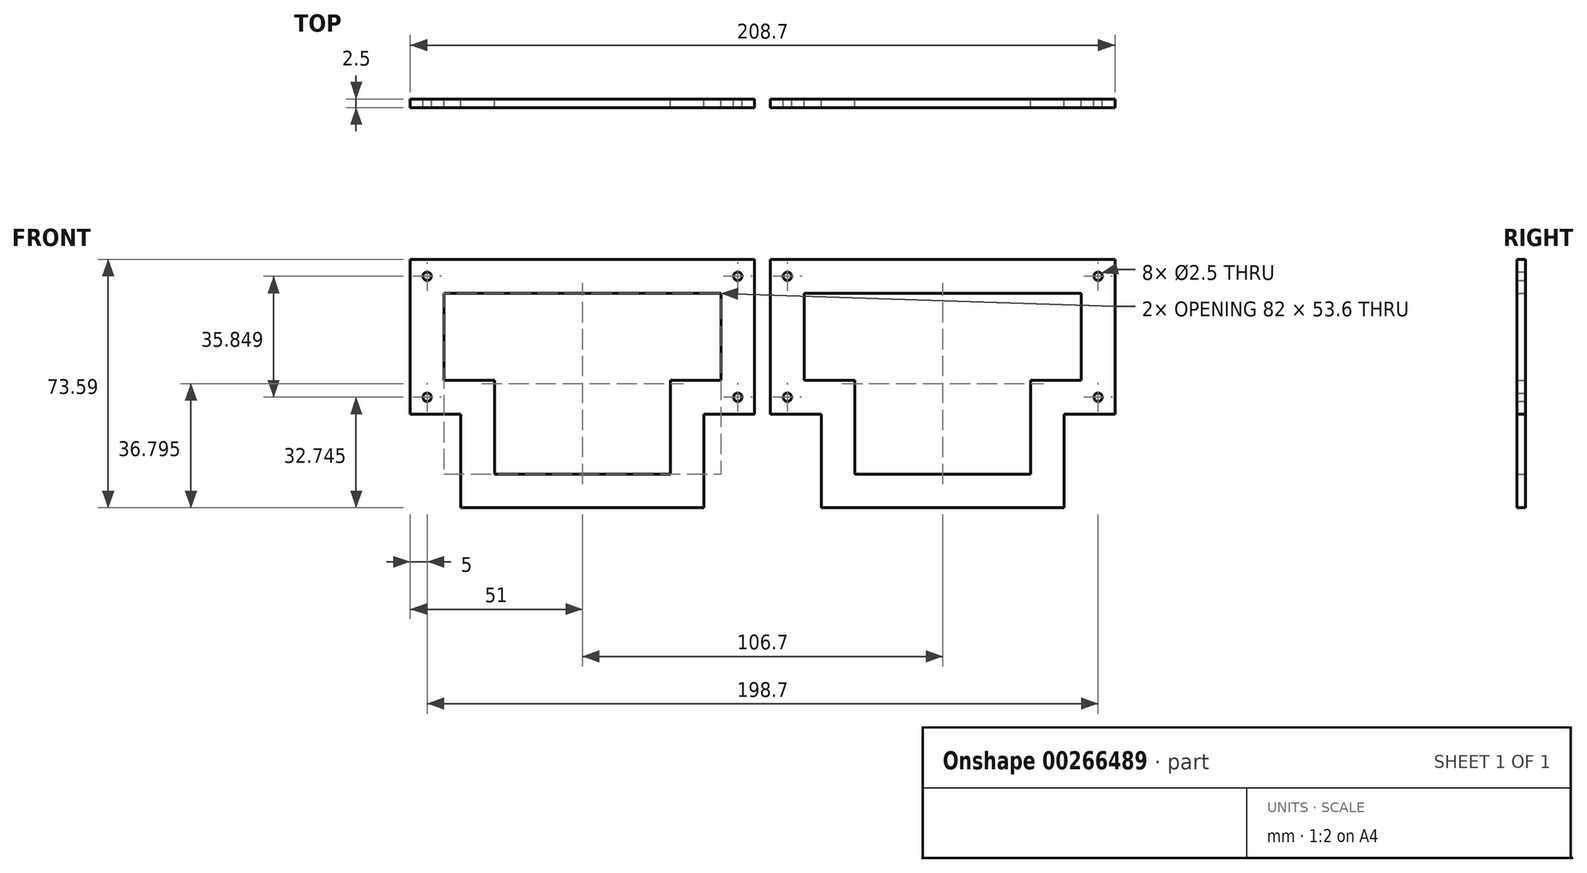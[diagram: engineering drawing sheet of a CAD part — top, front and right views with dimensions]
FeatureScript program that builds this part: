
annotation { "Feature Type Name" : "Feature", "Feature Type Description" : "" }
export const myFeature = defineFeature(function(context is Context, id is Id, definition is map)
    precondition{}
    {
        {
            var Q0;
            Q0=qCreatedBy(makeId("Front.planeOp"),FACE);
            var sketch = newSketch(context, id + "F0", { "sketchPlane" : qUnion([Q0])});
            skLineSegment(sketch, "E0", {"start": v(-36, -36.51) * mm, "end": v(36, -36.51) * mm});
            skLineSegment(sketch, "E1", {"start": v(36, -36.51) * mm, "end": v(36, -8.76) * mm});
            skLineSegment(sketch, "E2", {"start": v(36, -8.76) * mm, "end": v(51, -8.76) * mm});
            skLineSegment(sketch, "E3", {"start": v(51, -8.76) * mm, "end": v(51, 37.08) * mm});
            skLineSegment(sketch, "E4", {"start": v(51, 37.08) * mm, "end": v(-51, 37.08) * mm});
            skLineSegment(sketch, "E5", {"start": v(-51, 37.08) * mm, "end": v(-51, -8.76) * mm});
            skLineSegment(sketch, "E6", {"start": v(-51, -8.76) * mm, "end": v(-36, -8.76) * mm});
            skLineSegment(sketch, "E7", {"start": v(-36, -8.76) * mm, "end": v(-36, -36.51) * mm});
            skLineSegment(sketch, "E8.0", {"start": v(-26, -26.51) * mm, "end": v(26, -26.51) * mm});
            skLineSegment(sketch, "E8.1", {"start": v(-26, 1.24) * mm, "end": v(-26, -26.51) * mm});
            skLineSegment(sketch, "E8.2", {"start": v(26, -26.51) * mm, "end": v(26, 1.24) * mm});
            skLineSegment(sketch, "E8.3", {"start": v(-41, 1.24) * mm, "end": v(-26, 1.24) * mm});
            skLineSegment(sketch, "E8.4", {"start": v(26, 1.24) * mm, "end": v(41, 1.24) * mm});
            skLineSegment(sketch, "E8.5", {"start": v(41, 1.24) * mm, "end": v(41, 27.08) * mm});
            skLineSegment(sketch, "E8.6", {"start": v(41, 27.08) * mm, "end": v(-41, 27.08) * mm});
            skLineSegment(sketch, "E8.7", {"start": v(-41, 27.08) * mm, "end": v(-41, 1.24) * mm});
            skLineSegment(sketch, "E9", {"start": v(-51, 37.08) * mm, "end": v(-41, 27.08) * mm, "construction": true});
            skLineSegment(sketch, "E10", {"start": v(51, 37.08) * mm, "end": v(41, 27.08) * mm, "construction": true});
            skLineSegment(sketch, "E11", {"start": v(41, 1.24) * mm, "end": v(51, -8.76) * mm, "construction": true});
            skLineSegment(sketch, "E12", {"start": v(-41, 1.24) * mm, "end": v(-51, -8.76) * mm, "construction": true});
            skCircle(sketch, "E13", {"center": v(-46, 32.08) * mm, "radius": 1.25 * mm});
            skCircle(sketch, "E14", {"center": v(-46, -3.76) * mm, "radius": 1.25 * mm});
            skCircle(sketch, "E15", {"center": v(46, -3.76) * mm, "radius": 1.25 * mm});
            skCircle(sketch, "E16", {"center": v(46, 32.08) * mm, "radius": 1.25 * mm});
            skLineSegment(sketch, "E17.1.0.0", {"start": v(-132.7, 1.24) * mm, "end": v(-132.7, -26.51) * mm});
            skLineSegment(sketch, "E17.1.0.1", {"start": v(-132.7, -26.51) * mm, "end": v(-80.7, -26.51) * mm});
            skLineSegment(sketch, "E17.1.0.2", {"start": v(-65.7, 27.08) * mm, "end": v(-147.7, 27.08) * mm});
            skLineSegment(sketch, "E17.1.0.3", {"start": v(-142.7, -8.76) * mm, "end": v(-142.7, -36.51) * mm});
            skLineSegment(sketch, "E17.1.0.4", {"start": v(-147.7, 27.08) * mm, "end": v(-147.7, 1.24) * mm});
            skLineSegment(sketch, "E17.1.0.5", {"start": v(-65.7, 1.24) * mm, "end": v(-65.7, 27.08) * mm});
            skLineSegment(sketch, "E17.1.0.6", {"start": v(-70.7, -36.51) * mm, "end": v(-70.7, -8.76) * mm});
            skLineSegment(sketch, "E17.1.0.7", {"start": v(-157.7, 37.08) * mm, "end": v(-157.7, -8.76) * mm});
            skLineSegment(sketch, "E17.1.0.8", {"start": v(-142.7, -36.51) * mm, "end": v(-70.7, -36.51) * mm});
            skLineSegment(sketch, "E17.1.0.9", {"start": v(-80.7, -26.51) * mm, "end": v(-80.7, 1.24) * mm});
            skLineSegment(sketch, "E17.1.0.10", {"start": v(-147.7, 1.24) * mm, "end": v(-132.7, 1.24) * mm});
            skLineSegment(sketch, "E17.1.0.11", {"start": v(-80.7, 1.24) * mm, "end": v(-65.7, 1.24) * mm});
            skLineSegment(sketch, "E17.1.0.12", {"start": v(-147.7, 1.24) * mm, "end": v(-157.7, -8.76) * mm, "construction": true});
            skLineSegment(sketch, "E17.1.0.13", {"start": v(-70.7, -8.76) * mm, "end": v(-55.7, -8.76) * mm});
            skLineSegment(sketch, "E17.1.0.14", {"start": v(-157.7, -8.76) * mm, "end": v(-142.7, -8.76) * mm});
            skCircle(sketch, "E17.1.0.15", {"center": v(-152.7, 32.08) * mm, "radius": 1.25 * mm});
            skLineSegment(sketch, "E17.1.0.16", {"start": v(-157.7, 37.08) * mm, "end": v(-147.7, 27.08) * mm, "construction": true});
            skCircle(sketch, "E17.1.0.17", {"center": v(-152.7, -3.76) * mm, "radius": 1.25 * mm});
            skCircle(sketch, "E17.1.0.18", {"center": v(-60.7, -3.76) * mm, "radius": 1.25 * mm});
            skLineSegment(sketch, "E17.1.0.19", {"start": v(-65.7, 1.24) * mm, "end": v(-55.7, -8.76) * mm, "construction": true});
            skLineSegment(sketch, "E17.1.0.20", {"start": v(-55.7, -8.76) * mm, "end": v(-55.7, 37.08) * mm});
            skLineSegment(sketch, "E17.1.0.21", {"start": v(-55.7, 37.08) * mm, "end": v(-157.7, 37.08) * mm});
            skCircle(sketch, "E17.1.0.22", {"center": v(-60.7, 32.08) * mm, "radius": 1.25 * mm});
            skLineSegment(sketch, "E17.1.0.23", {"start": v(-55.7, 37.08) * mm, "end": v(-65.7, 27.08) * mm, "construction": true});
            skLineSegment(sketch, "E17.direction1", {"start": v(-36, -36.51) * mm, "end": v(-142.7, -36.51) * mm, "construction": true});
            skSolve(sketch);
        }
        {
            var Q0;
            Q0=makeQuery(id+"F0.imprint","IMPRINT",FACE,{"disambiguationData":[TD([[makeQuery(id+"F0.imprint","IMPRINT",EDGE,{"derivedFrom":sQuery(id+"F0.wireOp",EDGE,"E0")}),1.0]])]});
            var Q1;
            Q1=makeQuery(id+"F0.imprint","IMPRINT",FACE,{"disambiguationData":[TD([[makeQuery(id+"F0.imprint","IMPRINT",EDGE,{"derivedFrom":sQuery(id+"F0.wireOp",EDGE,"E17.1.0.0")}),-1.0]])]});
            extrude(context, id + "F1", {"entities" : qUnion([Q0, Q1]), "depth" : 2.5 * mm});
        }
    });
